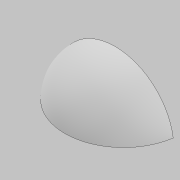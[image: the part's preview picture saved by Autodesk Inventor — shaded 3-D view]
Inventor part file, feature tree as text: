
AUTODESK INVENTOR PART (.ipt)
format: ipt  version: 2021 (Build 250183000, 183)  size: 120,320 bytes
history: native  units: mm
features: other x2, revolve x1, sketch x1
ambient origin geometry x8: Origin, YZ Plane, XZ Plane, XY Plane, X Axis, Y Axis, Z Axis, Center Point
bodies: Body1 (feature_tree)
feature tree (4):
  revolve  "Revolution2"  [1 undecoded]
  other  "end1"
  other  "end2"
  sketch  "Sketch1"  dims[d0=0.0mm d1=0.0mm d2=0.0mm d3=150.0mm d6=900.0mm d8=1039.230485mm d10=0.0mm d11=10.0mm d12=0.0mm d13=90.0deg d9=0.872665mm]
note: 1 required parameter value undecoded (feature->parameter linkage not recoverable at this tier; creation-order binding heuristic only, values carry confidence <= 0.55)
